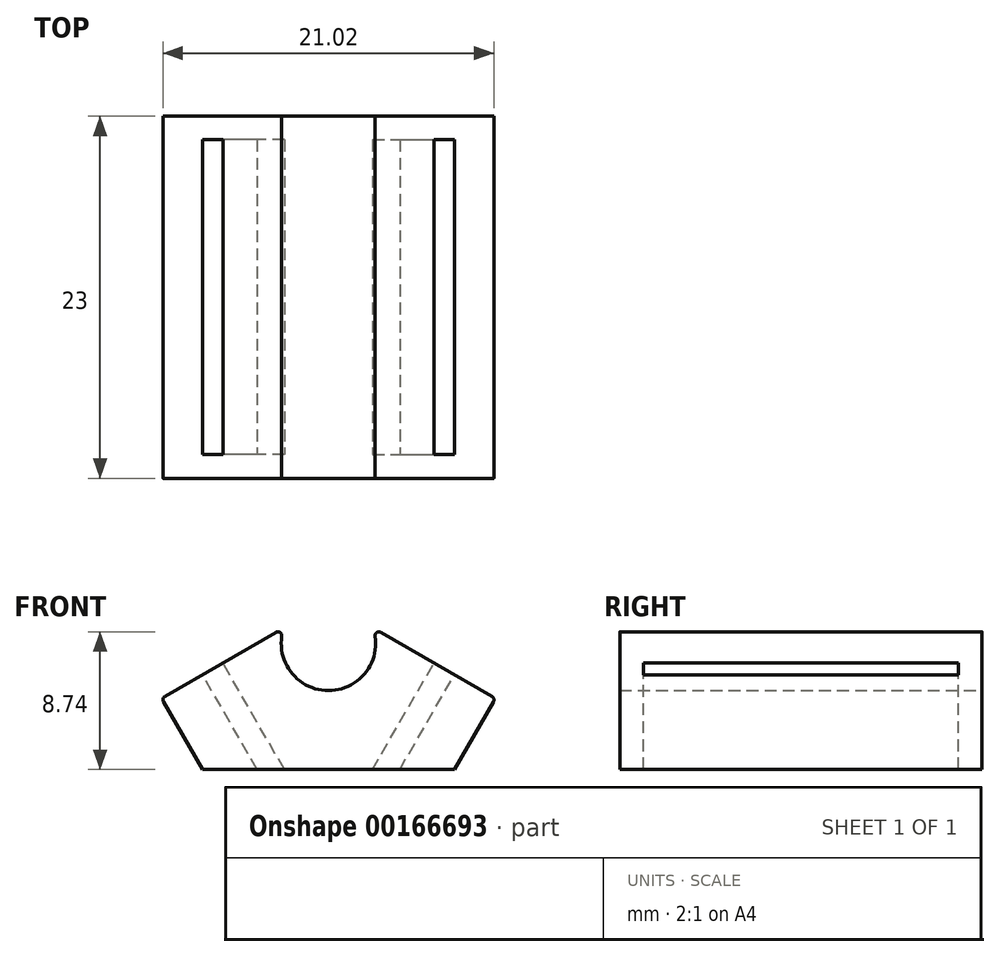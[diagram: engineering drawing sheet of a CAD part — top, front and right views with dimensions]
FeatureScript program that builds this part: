
annotation { "Feature Type Name" : "Feature", "Feature Type Description" : "" }
export const myFeature = defineFeature(function(context is Context, id is Id, definition is map)
    precondition{}
    {
        {
            assignVariable(context, id + "F0", {"name" : "length", "anyValue" : 23});
        }
        {
            var Q0;
            Q0=qCreatedBy(makeId("Front.planeOp"),FACE);
            var sketch = newSketch(context, id + "F1", { "sketchPlane" : qUnion([Q0])});
            skLineSegment(sketch, "E0", {"start": v(-8, 0) * mm, "end": v(-10.6, 4.51) * mm});
            skLineSegment(sketch, "E1", {"start": v(-10.6, 4.51) * mm, "end": v(-2.83, 9) * mm});
            skLineSegment(sketch, "E2", {"start": v(-8, 0) * mm, "end": v(0, 0) * mm});
            skLineSegment(sketch, "E3", {"start": v(0, 0) * mm, "end": v(0, 5) * mm});
            skArc(sketch, "E4", {"start": v(-2.83, 9) * mm, "mid": v(-2.45, 6.27) * mm, "end": v(0, 5) * mm});
            skSolve(sketch);
        }
        {
            var Q0;
            Q0 = qSketchRegion(id + "F1", true);
            extrude(context, id + "F2", {"entities" : qUnion([Q0]), "depth" : (getVariable(context, 'length')) * mm, "symmetric" : true});
        }
        {
            var Q0;
            Q0=makeQuery(id+"F2.opExtrude","SWEPT_FACE",FACE,{"disambiguationData":[OSD([sQuery(id+"F1.wireOp",EDGE,"E1")])]});
            cPlane(context, id + "F3", {"entities" : qUnion([Q0]), "cplaneType" : CPlaneType.OFFSET, "offset" : 0 * mm, "width" : 150 * mm, "height" : 150 * mm});
        }
        {
            var Q0;
            Q0=qCreatedBy(id+"F3.planeOp",FACE);
            var sketch = newSketch(context, id + "F4", { "sketchPlane" : qUnion([Q0])});
            skLineSegment(sketch, "E5.bottom", {"start": v(-2.43, 10) * mm, "end": v(-3.93, 10) * mm});
            skLineSegment(sketch, "E5.top", {"start": v(-2.43, -10) * mm, "end": v(-3.93, -10) * mm});
            skLineSegment(sketch, "E5.left", {"start": v(-2.43, 10) * mm, "end": v(-2.43, -10) * mm});
            skLineSegment(sketch, "E5.right", {"start": v(-3.93, 10) * mm, "end": v(-3.93, -10) * mm});
            skSolve(sketch);
        }
        {
            var Q0;
            Q0 = qSketchRegion(id + "F4", true);
            extrude(context, id + "F5", {"entities" : qUnion([Q0]), "operationType" : NewBodyOperationType.REMOVE, "oppositeDirection" : true, "depth" : 25 * mm});
        }
        {
            var Q0;
            Q0=makeQuery(id+"F2.opExtrude","SWEPT_EDGE",EDGE,{"disambiguationData":[OSD([sQuery(id+"F1.wireOp",EDGE,"E0"),sQuery(id+"F1.wireOp",EDGE,"E1")])]});
            var Q1;
            Q1=makeQuery(id+"F2.opExtrude","SWEPT_EDGE",EDGE,{"disambiguationData":[OSD([sQuery(id+"F1.wireOp",EDGE,"E1"),sQuery(id+"F1.wireOp",EDGE,"E4")])]});
            fillet(context, id + "F6", {"entities" : qUnion([Q0, Q1]), "radius" : 0.25 * mm, "tangentPropagation" : true, "allowEdgeOverflow" : false});
        }
        {
            var Q0;
            Q0=makeQuery(id+"F2.opExtrude","SWEPT_BODY",BODY,{"disambiguationData":[OSD([sQuery(id+"F1.wireOp",EDGE,"E0"),sQuery(id+"F1.wireOp",EDGE,"E1"),sQuery(id+"F1.wireOp",EDGE,"E2"),sQuery(id+"F1.wireOp",EDGE,"E3"),sQuery(id+"F1.wireOp",EDGE,"E4")])]});
            var Q1;
            Q1=qCreatedBy(makeId("Right.planeOp"),FACE);
            mirror(context, id + "F7", {"operationType" : NewBodyOperationType.ADD, "entities" : qUnion([Q0]), "mirrorPlane" : qUnion([Q1])});
        }
    });
